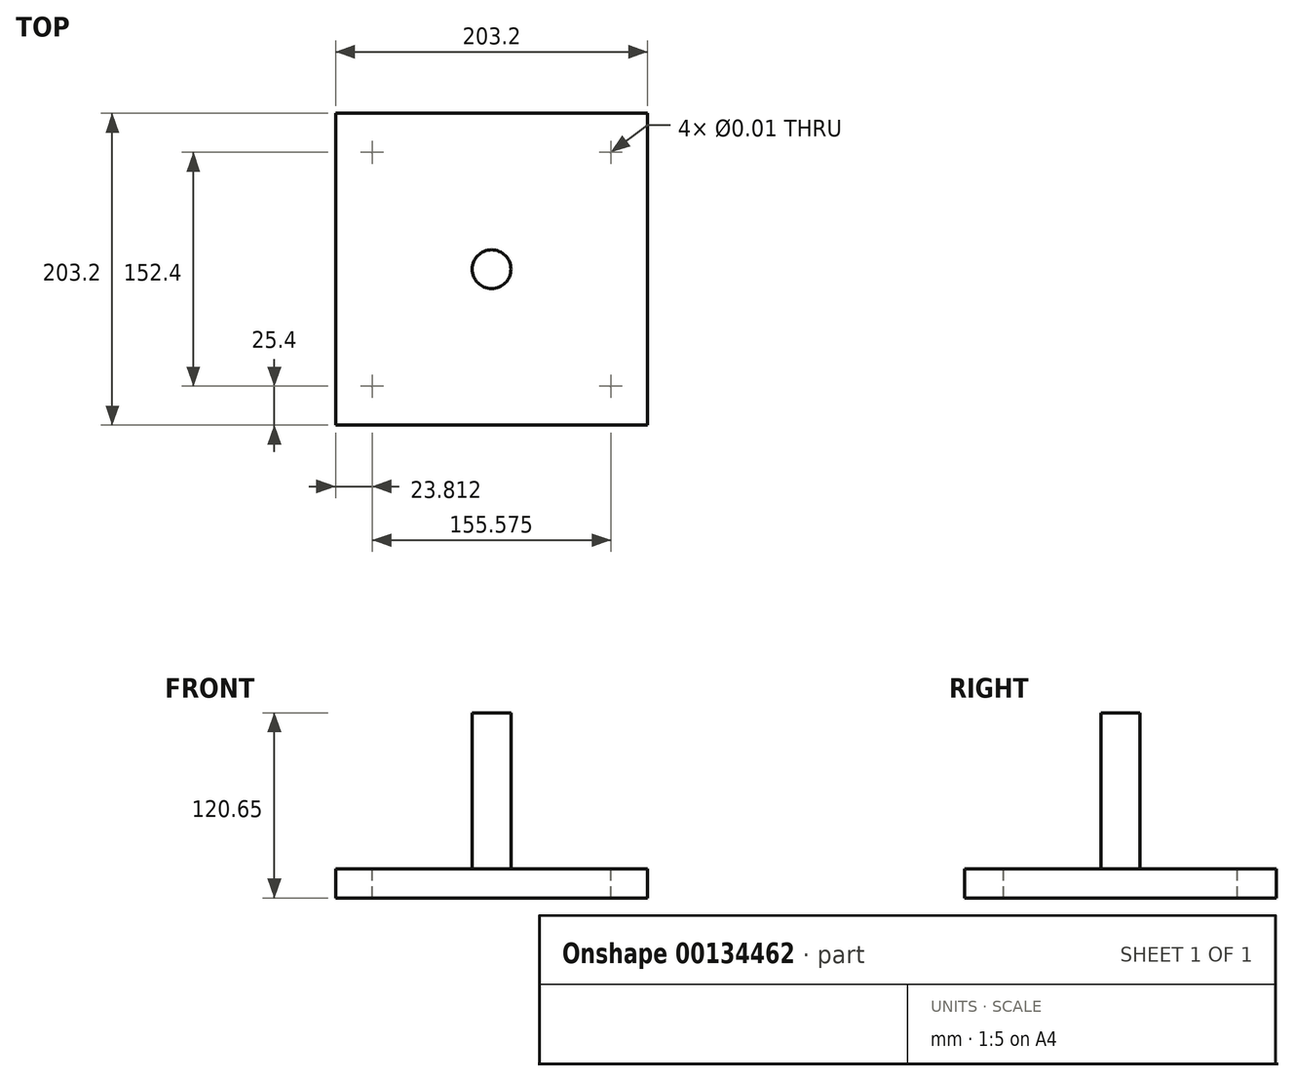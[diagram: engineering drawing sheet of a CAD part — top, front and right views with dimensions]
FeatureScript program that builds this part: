
annotation { "Feature Type Name" : "Feature", "Feature Type Description" : "" }
export const myFeature = defineFeature(function(context is Context, id is Id, definition is map)
    precondition{}
    {
        {
            var Q0;
            Q0=qCreatedBy(makeId("Top.planeOp"),FACE);
            var sketch = newSketch(context, id + "F0", { "sketchPlane" : qUnion([Q0])});
            skLineSegment(sketch, "E0.bottom", {"start": v(-101.6, -101.6) * mm, "end": v(101.6, -101.6) * mm});
            skLineSegment(sketch, "E0.top", {"start": v(-101.6, 101.6) * mm, "end": v(101.6, 101.6) * mm});
            skLineSegment(sketch, "E0.left", {"start": v(-101.6, -101.6) * mm, "end": v(-101.6, 101.6) * mm});
            skLineSegment(sketch, "E0.right", {"start": v(101.6, -101.6) * mm, "end": v(101.6, 101.6) * mm});
            skLineSegment(sketch, "E1", {"start": v(101.6, 101.6) * mm, "end": v(-101.6, -101.6) * mm, "construction": true});
            skSolve(sketch);
        }
        {
            var Q0;
            Q0=makeQuery(id+"F0.imprint","IMPRINT",FACE,{"disambiguationData":[TD([[makeQuery(id+"F0.imprint","IMPRINT",EDGE,{"derivedFrom":sQuery(id+"F0.wireOp",EDGE,"E0.bottom")}),1.0]])]});
            extrude(context, id + "F1", {"entities" : qUnion([Q0]), "depth" : 19.05 * mm});
        }
        {
            var Q0;
            Q0=makeQuery(id+"F1.opExtrude","CAP_FACE",FACE,{"disambiguationData":[OSD([sQuery(id+"F0.wireOp",EDGE,"E0.bottom"),sQuery(id+"F0.wireOp",EDGE,"E0.top"),sQuery(id+"F0.wireOp",EDGE,"E0.left"),sQuery(id+"F0.wireOp",EDGE,"E0.right")])],"isStart":false});
            var sketch = newSketch(context, id + "F2", { "sketchPlane" : qUnion([Q0])});
            skPoint(sketch, "E2", {"position": v(-77.79, 76.2) * mm});
            skPoint(sketch, "E3", {"position": v(-77.79, -76.2) * mm});
            skPoint(sketch, "E4", {"position": v(77.79, -76.2) * mm});
            skPoint(sketch, "E5", {"position": v(77.79, 76.2) * mm});
            skLineSegment(sketch, "E6", {"start": v(0, 101.6) * mm, "end": v(0, -101.6) * mm, "construction": true});
            skSolve(sketch);
        }
        {
            var Q0;
            Q0=sQuery(id+"F2.wireOp",VERTEX,"E2");
            var Q1;
            Q1=sQuery(id+"F2.wireOp",VERTEX,"E5");
            var Q2;
            Q2=sQuery(id+"F2.wireOp",VERTEX,"E3");
            var Q3;
            Q3=sQuery(id+"F2.wireOp",VERTEX,"E4");
            var Q4;
            Q4=makeQuery(id+"F1.opExtrude","SWEPT_BODY",BODY,{"disambiguationData":[OSD([sQuery(id+"F0.wireOp",EDGE,"E0.bottom"),sQuery(id+"F0.wireOp",EDGE,"E0.top"),sQuery(id+"F0.wireOp",EDGE,"E0.left"),sQuery(id+"F0.wireOp",EDGE,"E0.right")])]});
            hole(context, id + "F3", {"style" : HoleStyle.SIMPLE, "endStyle" : HoleEndStyle.THROUGH, "standardTappedOrClearance" : lookupTablePath({ "standard" : "ANSI", "size" : "3/8 (0.38)", "type" : "Drilled" }), "standardBlindInLast" : lookupTablePath({ "standard" : "ANSI", "size" : "3/8", "type" : "Drilled" }), "holeDiameter" : 3 / 203.2 * mm, "locations" : qUnion([Q0, Q1, Q2, Q3]), "scope" : qUnion([Q4]), "isTappedThrough" : true});
        }
        {
            var Q0;
            Q0=makeQuery(id+"F1.opExtrude","CAP_FACE",FACE,{"disambiguationData":[OSD([sQuery(id+"F0.wireOp",EDGE,"E0.bottom"),sQuery(id+"F0.wireOp",EDGE,"E0.top"),sQuery(id+"F0.wireOp",EDGE,"E0.left"),sQuery(id+"F0.wireOp",EDGE,"E0.right")])],"isStart":false});
            var sketch = newSketch(context, id + "F4", { "sketchPlane" : qUnion([Q0])});
            skCircle(sketch, "E7", {"center": v(0, 0) * mm, "radius": 12.64 * mm});
            skSolve(sketch);
        }
        {
            var Q0;
            Q0=makeQuery(id+"F4.imprint","IMPRINT",FACE,{"disambiguationData":[TD([[makeQuery(id+"F4.imprint","IMPRINT",EDGE,{"derivedFrom":sQuery(id+"F4.wireOp",EDGE,"E7")}),1.0]])]});
            extrude(context, id + "F5", {"entities" : qUnion([Q0]), "operationType" : NewBodyOperationType.ADD, "depth" : 101.6 * mm});
        }
    });
